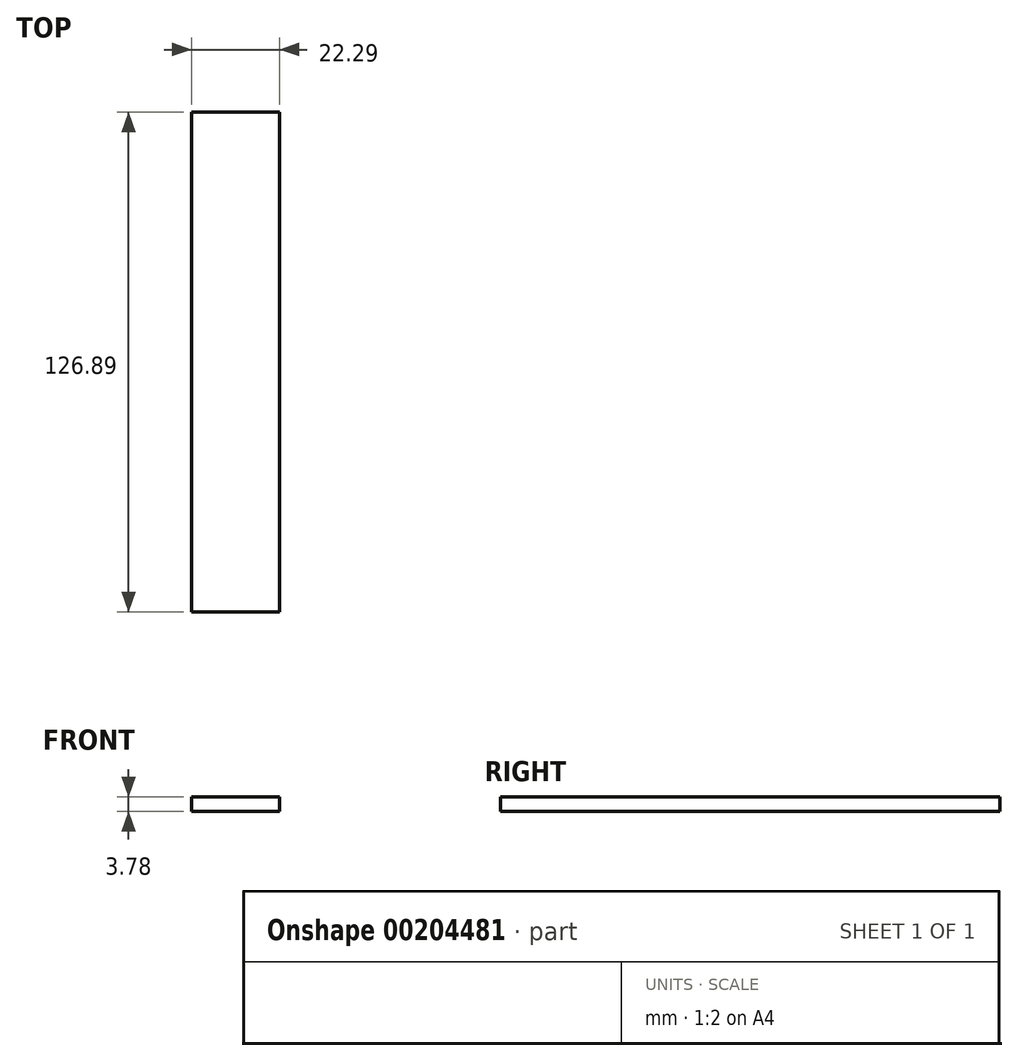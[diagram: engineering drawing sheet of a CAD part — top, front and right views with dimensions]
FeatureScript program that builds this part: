
annotation { "Feature Type Name" : "Feature", "Feature Type Description" : "" }
export const myFeature = defineFeature(function(context is Context, id is Id, definition is map)
    precondition{}
    {
        {
            var Q0;
            Q0=qCreatedBy(makeId("Front.planeOp"),FACE);
            var sketch = newSketch(context, id + "F0", { "sketchPlane" : qUnion([Q0])});
            skLineSegment(sketch, "E0", {"start": v(0, 0) * mm, "end": v(-22.3, 0) * mm});
            skLineSegment(sketch, "E1", {"start": v(-22.3, 0) * mm, "end": v(-22.3, -3.78) * mm});
            skLineSegment(sketch, "E2", {"start": v(-22.3, -3.78) * mm, "end": v(0, -3.67) * mm});
            skLineSegment(sketch, "E3", {"start": v(0, -3.67) * mm, "end": v(0, 0) * mm});
            skSolve(sketch);
        }
        {
            var Q0;
            Q0 = qSketchRegion(id + "F0", true);
            extrude(context, id + "F1", {"entities" : qUnion([Q0]), "depth" : 62.58 * mm});
        }
        {
            var Q0;
            Q0=makeQuery(id+"F1.opExtrude","CAP_FACE",FACE,{"disambiguationData":[OSD([sQuery(id+"F0.wireOp",EDGE,"E0"),sQuery(id+"F0.wireOp",EDGE,"E1"),sQuery(id+"F0.wireOp",EDGE,"E2"),sQuery(id+"F0.wireOp",EDGE,"E3")])],"isStart":true});
            extrude(context, id + "F2", {"entities" : qUnion([Q0]), "operationType" : NewBodyOperationType.ADD, "depth" : 64.31 * mm});
        }
    });
